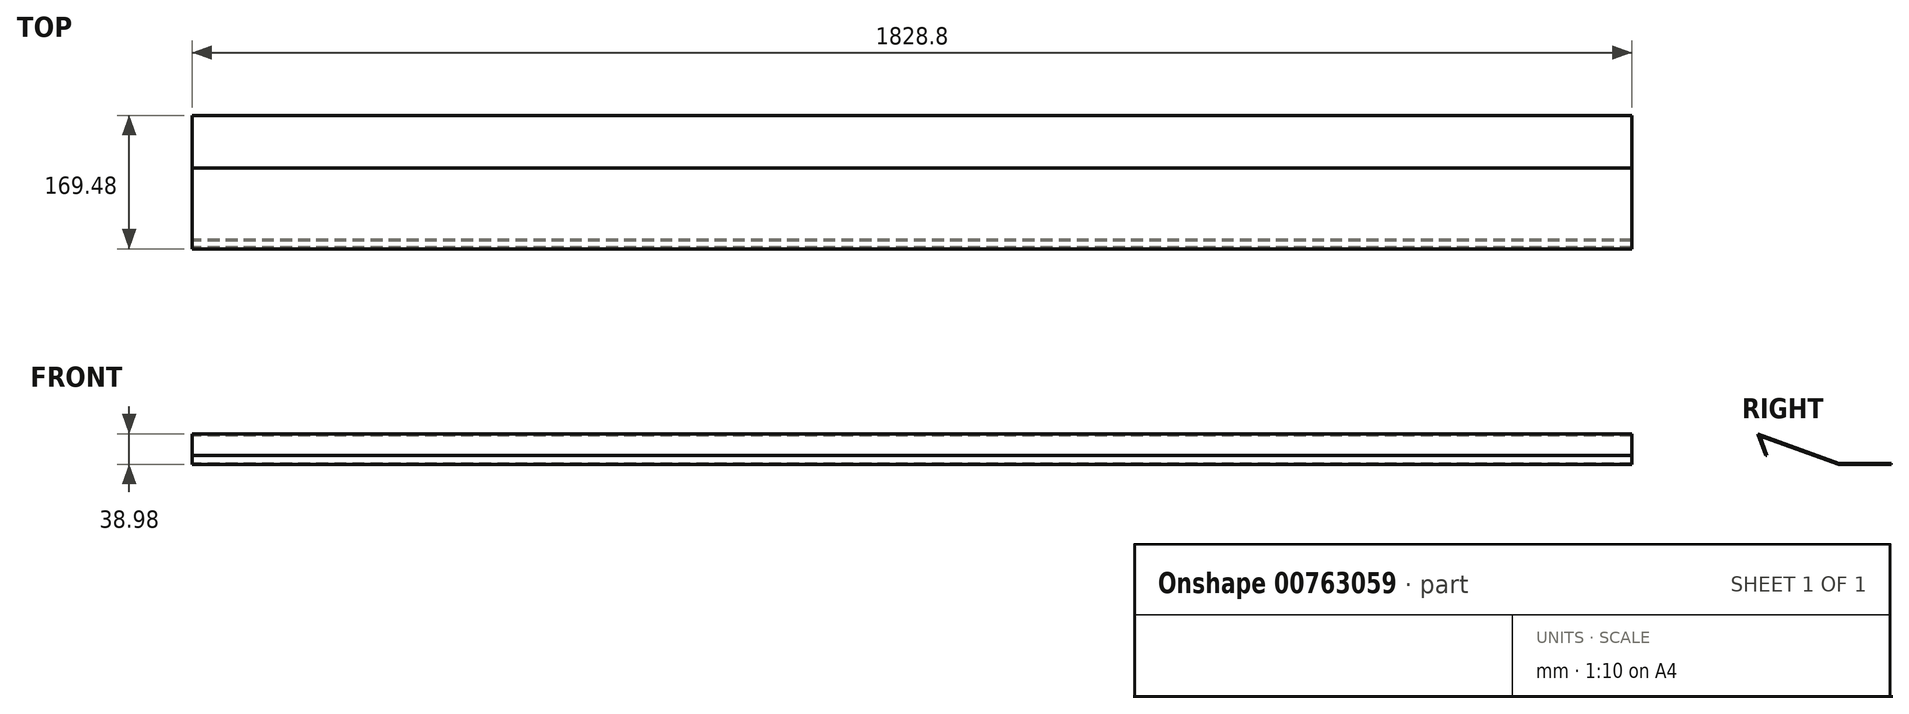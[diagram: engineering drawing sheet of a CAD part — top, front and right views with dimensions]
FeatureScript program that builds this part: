
annotation { "Feature Type Name" : "Feature", "Feature Type Description" : "" }
export const myFeature = defineFeature(function(context is Context, id is Id, definition is map)
    precondition{}
    {
        {
            var Q0;
            Q0=qCreatedBy(makeId("Right.planeOp"),FACE);
            var sketch = newSketch(context, id + "F0", { "sketchPlane" : qUnion([Q0])});
            skLineSegment(sketch, "E0", {"start": v(0, 0) * mm, "end": v(-66.55, 0) * mm});
            skLineSegment(sketch, "E1", {"start": v(-66.55, 0) * mm, "end": v(-169.48, 37.46) * mm});
            skLineSegment(sketch, "E2", {"start": v(-169.48, 37.46) * mm, "end": v(-159.37, 9.68) * mm});
            skLineSegment(sketch, "E3.0", {"start": v(0, -1.52) * mm, "end": v(-66.82, -1.52) * mm});
            skLineSegment(sketch, "E4.0", {"start": v(-66.82, -1.52) * mm, "end": v(-166.93, 34.91) * mm});
            skLineSegment(sketch, "E5.0", {"start": v(-166.93, 34.91) * mm, "end": v(-157.94, 10.2) * mm});
            skLineSegment(sketch, "E6", {"start": v(-159.37, 9.68) * mm, "end": v(-157.94, 10.2) * mm});
            skLineSegment(sketch, "E7", {"start": v(0, 0) * mm, "end": v(0, -1.52) * mm});
            skSolve(sketch);
        }
        {
            var Q0;
            Q0 = qSketchRegion(id + "F0", true);
            extrude(context, id + "F1", {"entities" : qUnion([Q0]), "endBound" : BoundingType.SYMMETRIC, "depth" : 1828.8 * mm, "offsetDistance" : 25.4 * mm});
        }
    });
